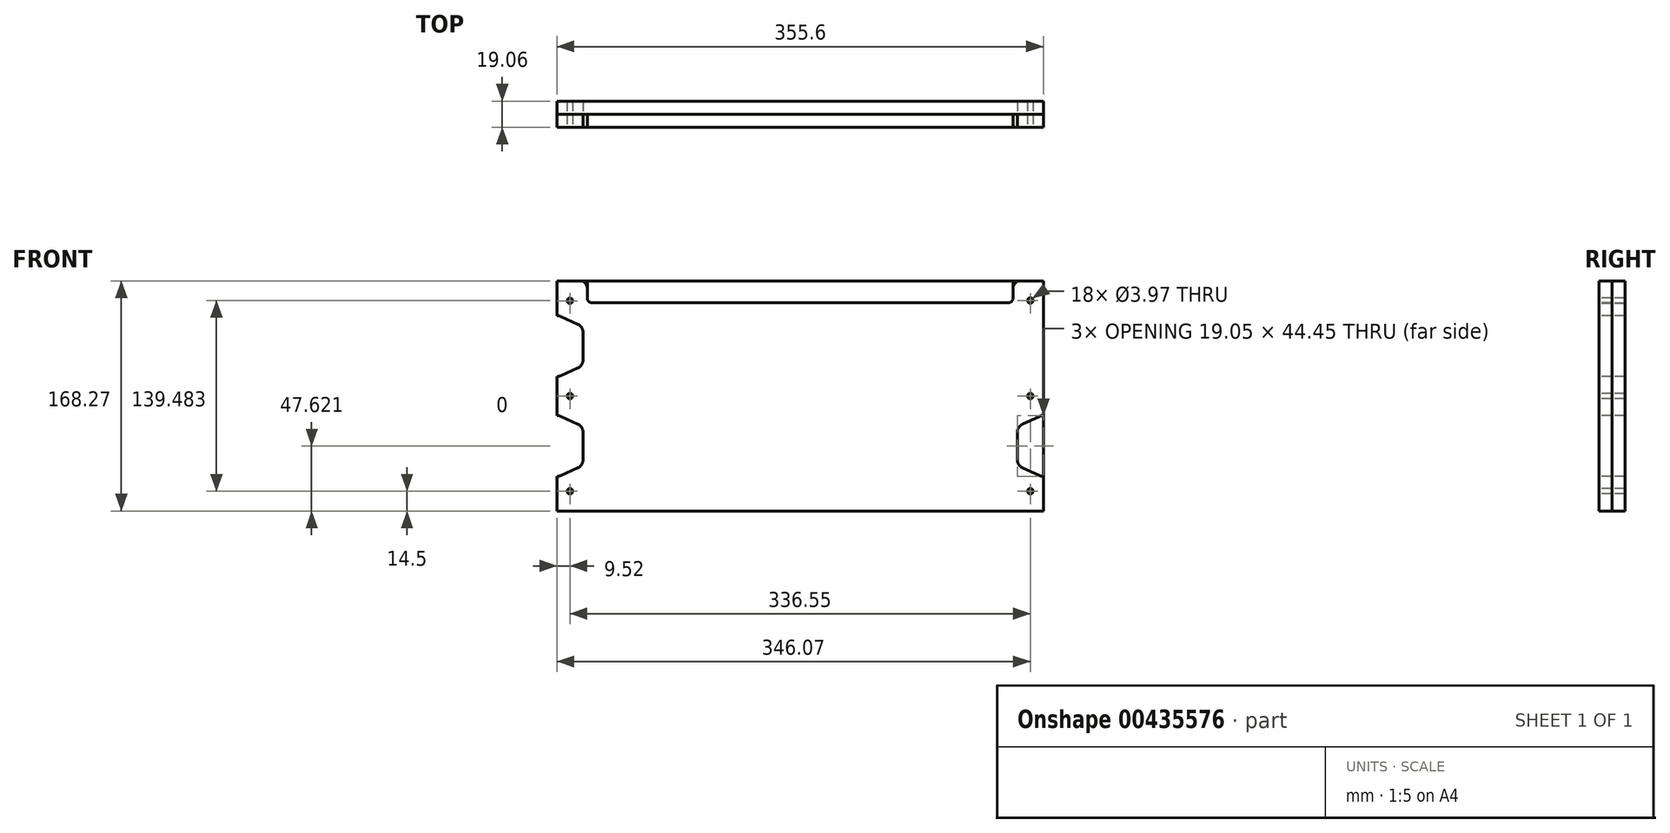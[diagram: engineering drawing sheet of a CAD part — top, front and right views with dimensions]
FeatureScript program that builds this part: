
annotation { "Feature Type Name" : "Feature", "Feature Type Description" : "" }
export const myFeature = defineFeature(function(context is Context, id is Id, definition is map)
    precondition{}
    {
        {
            var Q0;
            Q0=qCreatedBy(makeId("Front.planeOp"),FACE);
            var sketch = newSketch(context, id + "F0", { "sketchPlane" : qUnion([Q0])});
            skLineSegment(sketch, "E0", {"start": v(155.58, 21.72) * mm, "end": v(139.7, 21.72) * mm, "construction": true});
            skLineSegment(sketch, "E1", {"start": v(155.58, 25.32) * mm, "end": v(123.78, 10.87) * mm, "construction": true});
            skLineSegment(sketch, "E2", {"start": v(123.78, -11.9) * mm, "end": v(155.58, -26.34) * mm, "construction": true});
            skLineSegment(sketch, "E3", {"start": v(130.18, 21.72) * mm, "end": v(130.18, -29.08) * mm, "construction": true});
            skLineSegment(sketch, "E4", {"start": v(139.7, -22.73) * mm, "end": v(155.58, -22.73) * mm, "construction": true});
            skLineSegment(sketch, "E5", {"start": v(147.64, -35.43) * mm, "end": v(147.64, 28.07) * mm, "construction": true});
            skLineSegment(sketch, "E6", {"start": v(149.23, 28.07) * mm, "end": v(149.23, -35.43) * mm});
            skLineSegment(sketch, "E7", {"start": v(-184.15, 107.44) * mm, "end": v(-184.15, 120.14) * mm});
            skLineSegment(sketch, "E8", {"start": v(127, 107.44) * mm, "end": v(127, 120.14) * mm});
            skLineSegment(sketch, "E9", {"start": v(-180.97, 104.27) * mm, "end": v(123.83, 104.27) * mm});
            skLineSegment(sketch, "E10.bottom", {"start": v(-206.37, 120.14) * mm, "end": v(149.23, 120.14) * mm});
            skLineSegment(sketch, "E10.top", {"start": v(-206.37, -48.13) * mm, "end": v(149.23, -48.13) * mm});
            skLineSegment(sketch, "E10.left", {"start": v(-206.37, 120.14) * mm, "end": v(-206.37, -48.13) * mm});
            skLineSegment(sketch, "E10.right", {"start": v(149.23, 120.14) * mm, "end": v(149.23, -48.13) * mm});
            skLineSegment(sketch, "E11", {"start": v(-206.37, 36) * mm, "end": v(149.23, 36) * mm});
            skLineSegment(sketch, "E12", {"start": v(-28.57, 120.14) * mm, "end": v(-28.57, -48.13) * mm, "construction": true});
            skLineSegment(sketch, "E13", {"start": v(149.23, 21.72) * mm, "end": v(149.01, 21.72) * mm});
            skLineSegment(sketch, "E14", {"start": v(146.39, 21.15) * mm, "end": v(133.9, 15.47) * mm});
            skLineSegment(sketch, "E15", {"start": v(130.18, 9.69) * mm, "end": v(130.18, -10.7) * mm});
            skLineSegment(sketch, "E16", {"start": v(133.9, -16.49) * mm, "end": v(146.39, -22.16) * mm});
            skLineSegment(sketch, "E17", {"start": v(149.01, -22.73) * mm, "end": v(149.22, -22.73) * mm});
            skPoint(sketch, "E18.visualSharp", {"position": v(147.64, 21.72) * mm});
            skArc(sketch, "E18.filletArc", {"start": v(149.01, 21.72) * mm, "mid": v(147.67, 21.57) * mm, "end": v(146.39, 21.15) * mm});
            skPoint(sketch, "E19.visualSharp", {"position": v(130.18, 13.78) * mm});
            skArc(sketch, "E19.filletArc", {"start": v(133.9, 15.47) * mm, "mid": v(131.19, 13.13) * mm, "end": v(130.18, 9.69) * mm});
            skPoint(sketch, "E20.visualSharp", {"position": v(130.18, -14.8) * mm});
            skArc(sketch, "E20.filletArc", {"start": v(130.18, -10.7) * mm, "mid": v(131.19, -14.15) * mm, "end": v(133.9, -16.49) * mm});
            skPoint(sketch, "E21.visualSharp", {"position": v(147.64, -22.73) * mm});
            skArc(sketch, "E21.filletArc", {"start": v(146.39, -22.16) * mm, "mid": v(147.67, -22.59) * mm, "end": v(149.01, -22.73) * mm});
            skLineSegment(sketch, "E22.MirrorCS", {"start": v(-206.16, 94.74) * mm, "end": v(-206.37, 94.74) * mm});
            skArc(sketch, "E23.MirrorCS", {"start": v(-203.54, 94.17) * mm, "mid": v(-204.82, 94.6) * mm, "end": v(-206.16, 94.74) * mm});
            skArc(sketch, "E24.MirrorCS", {"start": v(-206.16, 50.3) * mm, "mid": v(-204.82, 50.44) * mm, "end": v(-203.54, 50.86) * mm});
            skLineSegment(sketch, "E25.MirrorCS", {"start": v(-206.38, 50.3) * mm, "end": v(-206.16, 50.3) * mm});
            skArc(sketch, "E26.MirrorCS", {"start": v(-191.05, 56.54) * mm, "mid": v(-188.34, 58.88) * mm, "end": v(-187.33, 62.32) * mm});
            skLineSegment(sketch, "E27.MirrorCS", {"start": v(-203.54, 50.86) * mm, "end": v(-191.05, 56.54) * mm});
            skLineSegment(sketch, "E28.MirrorCS", {"start": v(-187.33, 62.32) * mm, "end": v(-187.33, 82.71) * mm});
            skLineSegment(sketch, "E29.MirrorCS", {"start": v(-191.05, 88.5) * mm, "end": v(-203.54, 94.17) * mm});
            skArc(sketch, "E30.MirrorCS", {"start": v(-187.33, 82.71) * mm, "mid": v(-188.34, 86.15) * mm, "end": v(-191.05, 88.5) * mm});
            skLineSegment(sketch, "E31.MirrorCS", {"start": v(-206.38, 21.72) * mm, "end": v(-206.16, 21.72) * mm});
            skLineSegment(sketch, "E32.MirrorCS", {"start": v(-206.16, -22.73) * mm, "end": v(-206.37, -22.73) * mm});
            skArc(sketch, "E33.MirrorCS", {"start": v(-206.16, 21.72) * mm, "mid": v(-204.82, 21.57) * mm, "end": v(-203.54, 21.15) * mm});
            skArc(sketch, "E34.MirrorCS", {"start": v(-203.54, -22.16) * mm, "mid": v(-204.82, -22.59) * mm, "end": v(-206.16, -22.73) * mm});
            skLineSegment(sketch, "E35.MirrorCS", {"start": v(-187.33, 9.69) * mm, "end": v(-187.33, -10.7) * mm});
            skLineSegment(sketch, "E36.MirrorCS", {"start": v(-203.54, 21.15) * mm, "end": v(-191.05, 15.47) * mm});
            skArc(sketch, "E37.MirrorCS", {"start": v(-187.33, -10.7) * mm, "mid": v(-188.34, -14.15) * mm, "end": v(-191.05, -16.49) * mm});
            skLineSegment(sketch, "E38.MirrorCS", {"start": v(-191.05, -16.49) * mm, "end": v(-203.54, -22.16) * mm});
            skArc(sketch, "E39.MirrorCS", {"start": v(-191.05, 15.47) * mm, "mid": v(-188.34, 13.13) * mm, "end": v(-187.33, 9.69) * mm});
            skLineSegment(sketch, "E40.MirrorCS", {"start": v(149.23, 50.3) * mm, "end": v(149.01, 50.3) * mm});
            skLineSegment(sketch, "E41.MirrorCS", {"start": v(149.01, 94.74) * mm, "end": v(149.22, 94.74) * mm});
            skArc(sketch, "E42.MirrorCS", {"start": v(149.01, 50.3) * mm, "mid": v(147.67, 50.44) * mm, "end": v(146.39, 50.86) * mm});
            skArc(sketch, "E43.MirrorCS", {"start": v(146.39, 94.17) * mm, "mid": v(147.67, 94.6) * mm, "end": v(149.01, 94.74) * mm});
            skArc(sketch, "E44.MirrorCS", {"start": v(130.18, 82.71) * mm, "mid": v(131.19, 86.15) * mm, "end": v(133.9, 88.5) * mm});
            skArc(sketch, "E45.MirrorCS", {"start": v(133.9, 56.54) * mm, "mid": v(131.19, 58.88) * mm, "end": v(130.18, 62.32) * mm});
            skLineSegment(sketch, "E46.MirrorCS", {"start": v(130.18, 62.32) * mm, "end": v(130.18, 82.71) * mm});
            skLineSegment(sketch, "E47.MirrorCS", {"start": v(146.39, 50.86) * mm, "end": v(133.9, 56.54) * mm});
            skPoint(sketch, "E48.MirrorP", {"position": v(130.18, 58.23) * mm});
            skPoint(sketch, "E49.MirrorP", {"position": v(130.18, 86.8) * mm});
            skLineSegment(sketch, "E50.MirrorCS", {"start": v(133.9, 88.5) * mm, "end": v(146.39, 94.17) * mm});
            skPoint(sketch, "E51.MirrorP", {"position": v(147.64, 94.74) * mm});
            skLineSegment(sketch, "E52.MirrorCS", {"start": v(149.23, 47.12) * mm, "end": v(149.23, 110.62) * mm});
            skPoint(sketch, "E53.MirrorP", {"position": v(147.64, 50.3) * mm});
            skCircle(sketch, "E54", {"center": v(139.7, 105.85) * mm, "radius": 1.98 * mm});
            skCircle(sketch, "E55", {"center": v(139.7, 36) * mm, "radius": 1.98 * mm});
            skCircle(sketch, "E56.MirrorC", {"center": v(139.7, -33.63) * mm, "radius": 1.98 * mm});
            skCircle(sketch, "E57.MirrorC", {"center": v(-196.85, 105.64) * mm, "radius": 1.98 * mm});
            skCircle(sketch, "E58.MirrorC", {"center": v(-196.85, 36) * mm, "radius": 1.98 * mm});
            skCircle(sketch, "E59.MirrorC", {"center": v(-196.85, -33.63) * mm, "radius": 1.98 * mm});
            skPoint(sketch, "E60.visualSharp", {"position": v(-184.15, 104.27) * mm});
            skArc(sketch, "E60.filletArc", {"start": v(-184.15, 107.44) * mm, "mid": v(-183.22, 105.2) * mm, "end": v(-180.97, 104.27) * mm});
            skPoint(sketch, "E61.visualSharp", {"position": v(127, 104.27) * mm});
            skArc(sketch, "E61.filletArc", {"start": v(123.83, 104.27) * mm, "mid": v(126.07, 105.2) * mm, "end": v(127, 107.44) * mm});
            skSolve(sketch);
        }
        {
            var Q0;
            {var subQ15=sQuery(id+"F0.wireOp",EDGE,"E7");Q0=makeQuery(id+"F0.imprint","IMPRINT",FACE,{"disambiguationData":[TD([[makeQuery(id+"F0.imprint","IMPRINT",EDGE,{"derivedFrom":subQ15}),1.0]])]});}
            var Q1;
            {var subQ1=sQuery(id+"F0.wireOp",EDGE,"E10.top");Q1=makeQuery(id+"F0.imprint","IMPRINT",FACE,{"disambiguationData":[TD([[makeQuery(id+"F0.imprint","IMPRINT",EDGE,{"derivedFrom":subQ1}),1.0]])]});}
            var Q2;
            {var subQ0=sQuery(id+"F0.wireOp",EDGE,"E13");Q2=makeQuery(id+"F0.imprint","IMPRINT",FACE,{"disambiguationData":[TD([[makeQuery(id+"F0.imprint","IMPRINT",EDGE,{"derivedFrom":subQ0}),-1.0]])]});}
            var Q3;
            {var subQ0=sQuery(id+"F0.wireOp",EDGE,"E18.filletArc");var subQ3=sQuery(id+"F0.wireOp",EDGE,"E5");var subQ5=makeQuery(id+"F0.imprint","INTERSECT",VERTEX,{"derivedFrom":[subQ3,subQ0]});Q3=makeQuery(id+"F0.imprint","IMPRINT",FACE,{"disambiguationData":[TD([[makeQuery(id+"F0.imprint","IMPRINT",EDGE,{"disambiguationData":[TD([[subQ5,-1.0]])],"derivedFrom":subQ3}),-1.0]])]});}
            var Q4;
            {var subQ0=sQuery(id+"F0.wireOp",EDGE,"E1");var subQ1=makeQuery(id+"F0.imprint","IMPRINT",VERTEX,{"derivedFrom":subQ0});Q4=makeQuery(id+"F0.imprint","IMPRINT",FACE,{"disambiguationData":[TD([[makeQuery(id+"F0.imprint","IMPRINT",EDGE,{"disambiguationData":[TD([[subQ1,1.0]])],"derivedFrom":subQ0}),1.0]])]});}
            var Q5;
            {var subQ0=sQuery(id+"F0.wireOp",EDGE,"E19.filletArc");Q5=makeQuery(id+"F0.imprint","IMPRINT",FACE,{"disambiguationData":[TD([[makeQuery(id+"F0.imprint","IMPRINT",EDGE,{"derivedFrom":subQ0}),-1.0]])]});}
            var Q6;
            {var subQ0=sQuery(id+"F0.wireOp",EDGE,"E20.filletArc");Q6=makeQuery(id+"F0.imprint","IMPRINT",FACE,{"disambiguationData":[TD([[makeQuery(id+"F0.imprint","IMPRINT",EDGE,{"derivedFrom":subQ0}),-1.0]])]});}
            var Q7;
            {var subQ5=sQuery(id+"F0.wireOp",EDGE,"E17");Q7=makeQuery(id+"F0.imprint","IMPRINT",FACE,{"disambiguationData":[TD([[makeQuery(id+"F0.imprint","IMPRINT",EDGE,{"derivedFrom":subQ5}),-1.0]])]});}
            var Q8;
            {var subQ0=sQuery(id+"F0.wireOp",EDGE,"E21.filletArc");var subQ3=sQuery(id+"F0.wireOp",EDGE,"E5");var subQ5=makeQuery(id+"F0.imprint","INTERSECT",VERTEX,{"derivedFrom":[subQ3,subQ0]});Q8=makeQuery(id+"F0.imprint","IMPRINT",FACE,{"disambiguationData":[TD([[makeQuery(id+"F0.imprint","IMPRINT",EDGE,{"disambiguationData":[TD([[subQ5,1.0]])],"derivedFrom":subQ3}),-1.0]])]});}
            var Q9;
            {var subQ1=sQuery(id+"F0.wireOp",EDGE,"E2");var subQ3=sQuery(id+"F0.wireOp",EDGE,"E4");var subQ4=makeQuery(id+"F0.imprint","INTERSECT",VERTEX,{"derivedFrom":[subQ1,subQ3]});Q9=makeQuery(id+"F0.imprint","IMPRINT",FACE,{"disambiguationData":[TD([[makeQuery(id+"F0.imprint","IMPRINT",EDGE,{"disambiguationData":[TD([[subQ4,1.0]])],"derivedFrom":subQ1}),1.0]])]});}
            var Q10;
            {var subQ0=sQuery(id+"F0.wireOp",EDGE,"0a95d07e-ce51-44b1-ad99-18140d4708ba6.MirrorCS");var subQ1=makeQuery(id+"F0.imprint","INTERSECT",VERTEX,{"derivedFrom":[sQuery(id+"F0.wireOp",EDGE,"E43.MirrorCS"),subQ0]});Q10=makeQuery(id+"F0.imprint","IMPRINT",FACE,{"disambiguationData":[TD([[makeQuery(id+"F0.imprint","IMPRINT",EDGE,{"disambiguationData":[TD([[subQ1,1.0]])],"derivedFrom":subQ0}),1.0]])]});}
            var Q11;
            {var subQ0=sQuery(id+"F0.wireOp",EDGE,"E52.MirrorCS");var subQ1=sQuery(id+"F0.wireOp",EDGE,"0a95d07e-ce51-44b1-ad99-18140d4708ba8.MirrorCS");var subQ2=makeQuery(id+"F0.imprint","INTERSECT",VERTEX,{"derivedFrom":[subQ1,subQ0]});Q11=makeQuery(id+"F0.imprint","IMPRINT",FACE,{"disambiguationData":[TD([[makeQuery(id+"F0.imprint","IMPRINT",EDGE,{"disambiguationData":[TD([[subQ2,-1.0]])],"derivedFrom":subQ1}),-1.0]])]});}
            var Q12;
            {var subQ0=sQuery(id+"F0.wireOp",EDGE,"0a95d07e-ce51-44b1-ad99-18140d4708ba7.MirrorCS");var subQ5=makeQuery(id+"F0.imprint","IMPRINT",VERTEX,{"derivedFrom":subQ0});Q12=makeQuery(id+"F0.imprint","IMPRINT",FACE,{"disambiguationData":[TD([[makeQuery(id+"F0.imprint","IMPRINT",EDGE,{"disambiguationData":[TD([[subQ5,1.0]])],"derivedFrom":subQ0}),-1.0]])]});}
            var Q13;
            {var subQ0=sQuery(id+"F0.wireOp",EDGE,"0a95d07e-ce51-44b1-ad99-18140d4708ba6.MirrorCS");var subQ1=sQuery(id+"F0.wireOp",EDGE,"E43.MirrorCS");var subQ2=makeQuery(id+"F0.imprint","INTERSECT",VERTEX,{"derivedFrom":[subQ1,subQ0]});Q13=makeQuery(id+"F0.imprint","IMPRINT",FACE,{"disambiguationData":[TD([[makeQuery(id+"F0.imprint","IMPRINT",EDGE,{"disambiguationData":[TD([[subQ2,1.0]])],"derivedFrom":subQ1}),1.0]])]});}
            var Q14;
            {var subQ0=sQuery(id+"F0.wireOp",EDGE,"E44.MirrorCS");Q14=makeQuery(id+"F0.imprint","IMPRINT",FACE,{"disambiguationData":[TD([[makeQuery(id+"F0.imprint","IMPRINT",EDGE,{"derivedFrom":subQ0}),1.0]])]});}
            var Q15;
            {var subQ0=sQuery(id+"F0.wireOp",EDGE,"E45.MirrorCS");Q15=makeQuery(id+"F0.imprint","IMPRINT",FACE,{"disambiguationData":[TD([[makeQuery(id+"F0.imprint","IMPRINT",EDGE,{"derivedFrom":subQ0}),1.0]])]});}
            var Q16;
            {var subQ1=sQuery(id+"F0.wireOp",EDGE,"E42.MirrorCS");var subQ3=sQuery(id+"F0.wireOp",EDGE,"E418.MirrorCS");var subQ4=makeQuery(id+"F0.imprint","INTERSECT",VERTEX,{"derivedFrom":[subQ1,subQ3]});Q16=makeQuery(id+"F0.imprint","IMPRINT",FACE,{"disambiguationData":[TD([[makeQuery(id+"F0.imprint","IMPRINT",EDGE,{"disambiguationData":[TD([[subQ4,-1.0]])],"derivedFrom":subQ1}),1.0]])]});}
            var Q17;
            {var subQ0=sQuery(id+"F0.wireOp",EDGE,"0a95d07e-ce51-44b1-ad99-18140d4708ba9.MirrorCS");var subQ1=sQuery(id+"F0.wireOp",EDGE,"E42.MirrorCS");var subQ2=makeQuery(id+"F0.imprint","INTERSECT",VERTEX,{"derivedFrom":[subQ1,subQ0]});Q17=makeQuery(id+"F0.imprint","IMPRINT",FACE,{"disambiguationData":[TD([[makeQuery(id+"F0.imprint","IMPRINT",EDGE,{"disambiguationData":[TD([[subQ2,-1.0]])],"derivedFrom":subQ1}),1.0]])]});}
            extrude(context, id + "F1", {"entities" : qUnion([Q0, Q1, Q2, Q3, Q4, Q5, Q6, Q7, Q8, Q9, Q10, Q11, Q12, Q13, Q14, Q15, Q16, Q17]), "depth" : 9.52 * mm});
        }
        {
            var Q0;
            {var subQ1=sQuery(id+"F0.wireOp",EDGE,"E10.top");Q0=makeQuery(id+"F0.imprint","IMPRINT",FACE,{"disambiguationData":[TD([[makeQuery(id+"F0.imprint","IMPRINT",EDGE,{"derivedFrom":subQ1}),1.0]])]});}
            var Q1;
            {var subQ15=sQuery(id+"F0.wireOp",EDGE,"E7");Q1=makeQuery(id+"F0.imprint","IMPRINT",FACE,{"disambiguationData":[TD([[makeQuery(id+"F0.imprint","IMPRINT",EDGE,{"derivedFrom":subQ15}),1.0]])]});}
            var Q2;
            {var subQ1=sQuery(id+"F0.wireOp",EDGE,"E7");Q2=makeQuery(id+"F0.imprint","IMPRINT",FACE,{"disambiguationData":[TD([[makeQuery(id+"F0.imprint","IMPRINT",EDGE,{"derivedFrom":subQ1}),-1.0]])]});}
            var Q3;
            {var subQ0=sQuery(id+"F0.wireOp",EDGE,"E20.filletArc");Q3=makeQuery(id+"F0.imprint","IMPRINT",FACE,{"disambiguationData":[TD([[makeQuery(id+"F0.imprint","IMPRINT",EDGE,{"derivedFrom":subQ0}),-1.0]])]});}
            var Q4;
            {var subQ5=sQuery(id+"F0.wireOp",EDGE,"E17");Q4=makeQuery(id+"F0.imprint","IMPRINT",FACE,{"disambiguationData":[TD([[makeQuery(id+"F0.imprint","IMPRINT",EDGE,{"derivedFrom":subQ5}),-1.0]])]});}
            var Q5;
            {var subQ0=sQuery(id+"F0.wireOp",EDGE,"E21.filletArc");var subQ3=sQuery(id+"F0.wireOp",EDGE,"E5");var subQ5=makeQuery(id+"F0.imprint","INTERSECT",VERTEX,{"derivedFrom":[subQ3,subQ0]});Q5=makeQuery(id+"F0.imprint","IMPRINT",FACE,{"disambiguationData":[TD([[makeQuery(id+"F0.imprint","IMPRINT",EDGE,{"disambiguationData":[TD([[subQ5,1.0]])],"derivedFrom":subQ3}),-1.0]])]});}
            var Q6;
            {var subQ1=sQuery(id+"F0.wireOp",EDGE,"E2");var subQ3=sQuery(id+"F0.wireOp",EDGE,"E4");var subQ4=makeQuery(id+"F0.imprint","INTERSECT",VERTEX,{"derivedFrom":[subQ1,subQ3]});Q6=makeQuery(id+"F0.imprint","IMPRINT",FACE,{"disambiguationData":[TD([[makeQuery(id+"F0.imprint","IMPRINT",EDGE,{"disambiguationData":[TD([[subQ4,1.0]])],"derivedFrom":subQ1}),1.0]])]});}
            var Q7;
            {var subQ0=sQuery(id+"F0.wireOp",EDGE,"E19.filletArc");Q7=makeQuery(id+"F0.imprint","IMPRINT",FACE,{"disambiguationData":[TD([[makeQuery(id+"F0.imprint","IMPRINT",EDGE,{"derivedFrom":subQ0}),-1.0]])]});}
            var Q8;
            {var subQ0=sQuery(id+"F0.wireOp",EDGE,"E1");var subQ1=makeQuery(id+"F0.imprint","IMPRINT",VERTEX,{"derivedFrom":subQ0});Q8=makeQuery(id+"F0.imprint","IMPRINT",FACE,{"disambiguationData":[TD([[makeQuery(id+"F0.imprint","IMPRINT",EDGE,{"disambiguationData":[TD([[subQ1,1.0]])],"derivedFrom":subQ0}),1.0]])]});}
            var Q9;
            {var subQ0=sQuery(id+"F0.wireOp",EDGE,"E18.filletArc");var subQ3=sQuery(id+"F0.wireOp",EDGE,"E5");var subQ5=makeQuery(id+"F0.imprint","INTERSECT",VERTEX,{"derivedFrom":[subQ3,subQ0]});Q9=makeQuery(id+"F0.imprint","IMPRINT",FACE,{"disambiguationData":[TD([[makeQuery(id+"F0.imprint","IMPRINT",EDGE,{"disambiguationData":[TD([[subQ5,-1.0]])],"derivedFrom":subQ3}),-1.0]])]});}
            var Q10;
            {var subQ0=sQuery(id+"F0.wireOp",EDGE,"E13");Q10=makeQuery(id+"F0.imprint","IMPRINT",FACE,{"disambiguationData":[TD([[makeQuery(id+"F0.imprint","IMPRINT",EDGE,{"derivedFrom":subQ0}),-1.0]])]});}
            var Q11;
            {var subQ0=sQuery(id+"F0.wireOp",EDGE,"E52.MirrorCS");var subQ1=sQuery(id+"F0.wireOp",EDGE,"0a95d07e-ce51-44b1-ad99-18140d4708ba8.MirrorCS");var subQ2=makeQuery(id+"F0.imprint","INTERSECT",VERTEX,{"derivedFrom":[subQ1,subQ0]});Q11=makeQuery(id+"F0.imprint","IMPRINT",FACE,{"disambiguationData":[TD([[makeQuery(id+"F0.imprint","IMPRINT",EDGE,{"disambiguationData":[TD([[subQ2,-1.0]])],"derivedFrom":subQ1}),-1.0]])]});}
            var Q12;
            {var subQ0=sQuery(id+"F0.wireOp",EDGE,"0a95d07e-ce51-44b1-ad99-18140d4708ba6.MirrorCS");var subQ1=makeQuery(id+"F0.imprint","INTERSECT",VERTEX,{"derivedFrom":[sQuery(id+"F0.wireOp",EDGE,"E43.MirrorCS"),subQ0]});Q12=makeQuery(id+"F0.imprint","IMPRINT",FACE,{"disambiguationData":[TD([[makeQuery(id+"F0.imprint","IMPRINT",EDGE,{"disambiguationData":[TD([[subQ1,1.0]])],"derivedFrom":subQ0}),1.0]])]});}
            var Q13;
            Q13=makeQuery(id+"F1.opExtrude","CAP_FACE",FACE,{"disambiguationData":[OSD([sQuery(id+"F0.wireOp",EDGE,"E6"),sQuery(id+"F0.wireOp",EDGE,"E7"),sQuery(id+"F0.wireOp",EDGE,"E8"),sQuery(id+"F0.wireOp",EDGE,"E9"),sQuery(id+"F0.wireOp",EDGE,"E10.bottom"),sQuery(id+"F0.wireOp",EDGE,"E10.top"),sQuery(id+"F0.wireOp",EDGE,"E10.right"),sQuery(id+"F0.wireOp",EDGE,"E13"),sQuery(id+"F0.wireOp",EDGE,"E14"),sQuery(id+"F0.wireOp",EDGE,"E15"),sQuery(id+"F0.wireOp",EDGE,"E16"),sQuery(id+"F0.wireOp",EDGE,"E17"),sQuery(id+"F0.wireOp",EDGE,"E18.filletArc"),sQuery(id+"F0.wireOp",EDGE,"E19.filletArc"),sQuery(id+"F0.wireOp",EDGE,"E20.filletArc"),sQuery(id+"F0.wireOp",EDGE,"E21.filletArc"),sQuery(id+"F0.wireOp",EDGE,"E22.MirrorCS"),sQuery(id+"F0.wireOp",EDGE,"E23.MirrorCS"),sQuery(id+"F0.wireOp",EDGE,"E24.MirrorCS"),sQuery(id+"F0.wireOp",EDGE,"E25.MirrorCS"),sQuery(id+"F0.wireOp",EDGE,"E26.MirrorCS"),sQuery(id+"F0.wireOp",EDGE,"E27.MirrorCS"),sQuery(id+"F0.wireOp",EDGE,"E28.MirrorCS"),sQuery(id+"F0.wireOp",EDGE,"E10.left"),sQuery(id+"F0.wireOp",EDGE,"E29.MirrorCS"),sQuery(id+"F0.wireOp",EDGE,"E30.MirrorCS"),sQuery(id+"F0.wireOp",EDGE,"E31.MirrorCS"),sQuery(id+"F0.wireOp",EDGE,"E32.MirrorCS"),sQuery(id+"F0.wireOp",EDGE,"E33.MirrorCS"),sQuery(id+"F0.wireOp",EDGE,"E34.MirrorCS"),sQuery(id+"F0.wireOp",EDGE,"E35.MirrorCS"),sQuery(id+"F0.wireOp",EDGE,"E36.MirrorCS"),sQuery(id+"F0.wireOp",EDGE,"E37.MirrorCS"),sQuery(id+"F0.wireOp",EDGE,"E38.MirrorCS"),sQuery(id+"F0.wireOp",EDGE,"E39.MirrorCS"),sQuery(id+"F0.wireOp",EDGE,"E42.MirrorCS"),sQuery(id+"F0.wireOp",EDGE,"E43.MirrorCS"),sQuery(id+"F0.wireOp",EDGE,"E44.MirrorCS"),sQuery(id+"F0.wireOp",EDGE,"E45.MirrorCS"),sQuery(id+"F0.wireOp",EDGE,"0a95d07e-ce51-44b1-ad99-18140d4708ba6.MirrorCS"),sQuery(id+"F0.wireOp",EDGE,"0a95d07e-ce51-44b1-ad99-18140d4708ba9.MirrorCS"),sQuery(id+"F0.wireOp",EDGE,"E47.MirrorCS"),sQuery(id+"F0.wireOp",EDGE,"E50.MirrorCS"),sQuery(id+"F0.wireOp",EDGE,"E52.MirrorCS"),sQuery(id+"F0.wireOp",EDGE,"E417.MirrorCS"),sQuery(id+"F0.wireOp",EDGE,"E54"),sQuery(id+"F0.wireOp",EDGE,"E55"),sQuery(id+"F0.wireOp",EDGE,"E56.MirrorC"),sQuery(id+"F0.wireOp",EDGE,"E57.MirrorC"),sQuery(id+"F0.wireOp",EDGE,"E58.MirrorC"),sQuery(id+"F0.wireOp",EDGE,"E59.MirrorC"),sQuery(id+"F0.wireOp",EDGE,"E60.filletArc"),sQuery(id+"F0.wireOp",EDGE,"E61.filletArc")])],"isStart":false});
            var Q14;
            {var subQ1=sQuery(id+"F0.wireOp",EDGE,"E42.MirrorCS");var subQ3=sQuery(id+"F0.wireOp",EDGE,"E418.MirrorCS");var subQ4=makeQuery(id+"F0.imprint","INTERSECT",VERTEX,{"derivedFrom":[subQ1,subQ3]});Q14=makeQuery(id+"F0.imprint","IMPRINT",FACE,{"disambiguationData":[TD([[makeQuery(id+"F0.imprint","IMPRINT",EDGE,{"disambiguationData":[TD([[subQ4,-1.0]])],"derivedFrom":subQ1}),1.0]])]});}
            var Q15;
            {var subQ0=sQuery(id+"F0.wireOp",EDGE,"0a95d07e-ce51-44b1-ad99-18140d4708ba9.MirrorCS");var subQ1=sQuery(id+"F0.wireOp",EDGE,"E42.MirrorCS");var subQ2=makeQuery(id+"F0.imprint","INTERSECT",VERTEX,{"derivedFrom":[subQ1,subQ0]});Q15=makeQuery(id+"F0.imprint","IMPRINT",FACE,{"disambiguationData":[TD([[makeQuery(id+"F0.imprint","IMPRINT",EDGE,{"disambiguationData":[TD([[subQ2,-1.0]])],"derivedFrom":subQ1}),1.0]])]});}
            var Q16;
            {var subQ0=sQuery(id+"F0.wireOp",EDGE,"E45.MirrorCS");Q16=makeQuery(id+"F0.imprint","IMPRINT",FACE,{"disambiguationData":[TD([[makeQuery(id+"F0.imprint","IMPRINT",EDGE,{"derivedFrom":subQ0}),1.0]])]});}
            var Q17;
            {var subQ0=sQuery(id+"F0.wireOp",EDGE,"E44.MirrorCS");Q17=makeQuery(id+"F0.imprint","IMPRINT",FACE,{"disambiguationData":[TD([[makeQuery(id+"F0.imprint","IMPRINT",EDGE,{"derivedFrom":subQ0}),1.0]])]});}
            var Q18;
            {var subQ0=sQuery(id+"F0.wireOp",EDGE,"0a95d07e-ce51-44b1-ad99-18140d4708ba7.MirrorCS");var subQ5=makeQuery(id+"F0.imprint","IMPRINT",VERTEX,{"derivedFrom":subQ0});Q18=makeQuery(id+"F0.imprint","IMPRINT",FACE,{"disambiguationData":[TD([[makeQuery(id+"F0.imprint","IMPRINT",EDGE,{"disambiguationData":[TD([[subQ5,1.0]])],"derivedFrom":subQ0}),-1.0]])]});}
            var Q19;
            {var subQ0=sQuery(id+"F0.wireOp",EDGE,"0a95d07e-ce51-44b1-ad99-18140d4708ba6.MirrorCS");var subQ1=sQuery(id+"F0.wireOp",EDGE,"E43.MirrorCS");var subQ2=makeQuery(id+"F0.imprint","INTERSECT",VERTEX,{"derivedFrom":[subQ1,subQ0]});Q19=makeQuery(id+"F0.imprint","IMPRINT",FACE,{"disambiguationData":[TD([[makeQuery(id+"F0.imprint","IMPRINT",EDGE,{"disambiguationData":[TD([[subQ2,1.0]])],"derivedFrom":subQ1}),1.0]])]});}
            extrude(context, id + "F2", {"entities" : qUnion([Q0, Q1, Q2, Q3, Q4, Q5, Q6, Q7, Q8, Q9, Q10, Q11, Q12, Q13, Q14, Q15, Q16, Q17, Q18, Q19]), "operationType" : NewBodyOperationType.ADD, "oppositeDirection" : true, "depth" : 9.52 * mm});
        }
        {
            var Q0;
            Q0=makeQuery(id+"F1.opExtrude","SWEPT_EDGE",EDGE,{"disambiguationData":[OSD([sQuery(id+"F0.wireOp",EDGE,"E7"),sQuery(id+"F0.wireOp",EDGE,"E10.bottom")])]});
            var Q1;
            Q1=makeQuery(id+"F1.opExtrude","SWEPT_EDGE",EDGE,{"disambiguationData":[OSD([sQuery(id+"F0.wireOp",EDGE,"E8"),sQuery(id+"F0.wireOp",EDGE,"E10.bottom")])]});
            chamfer(context, id + "F3", {"entities" : qUnion([Q0, Q1]), "width" : 3.17 * mm, "tangentPropagation" : true});
        }
        {
            var Q0;
            {var subQ0=sQuery(id+"F0.wireOp",EDGE,"E7");Q0=makeQuery(id+"F3.opChamfer","BLEND_EDGE",EDGE,{"blendedFrom":[makeQuery(id+"F1.opExtrude","SWEPT_EDGE",EDGE,{"disambiguationData":[OSD([subQ0,sQuery(id+"F0.wireOp",EDGE,"E10.bottom")])]}),makeQuery(id+"F1.opExtrude","SWEPT_FACE",FACE,{"disambiguationData":[OSD([subQ0])]})],"blendedInto":[makeQuery(id+"F1.opExtrude","SWEPT_FACE",FACE,{"disambiguationData":[OSD([subQ0])]})]});}
            var Q1;
            {var subQ0=sQuery(id+"F0.wireOp",EDGE,"E8");Q1=makeQuery(id+"F3.opChamfer","BLEND_EDGE",EDGE,{"blendedFrom":[makeQuery(id+"F1.opExtrude","SWEPT_EDGE",EDGE,{"disambiguationData":[OSD([subQ0,sQuery(id+"F0.wireOp",EDGE,"E10.bottom")])]}),makeQuery(id+"F1.opExtrude","SWEPT_FACE",FACE,{"disambiguationData":[OSD([subQ0])]})],"blendedInto":[makeQuery(id+"F1.opExtrude","SWEPT_FACE",FACE,{"disambiguationData":[OSD([subQ0])]})]});}
            fillet(context, id + "F4", {"entities" : qUnion([Q0, Q1]), "radius" : 6.35 * mm, "tangentPropagation" : true, "allowEdgeOverflow" : false});
        }
    });
